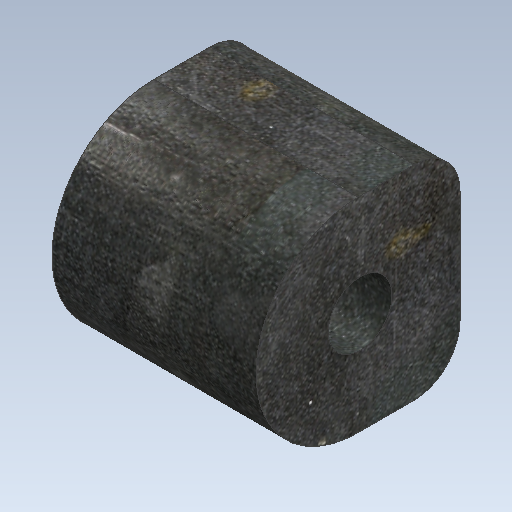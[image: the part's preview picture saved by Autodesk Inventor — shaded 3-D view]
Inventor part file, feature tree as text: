
AUTODESK INVENTOR PART (.ipt)
format: ipt  version: 2021 (Build 250183000, 183)  size: 340,992 bytes
history: native  units: mm
features: extrude x2, fillet x2, sketch x2
ambient origin geometry x8: Origin, YZ Plane, XZ Plane, XY Plane, X Axis, Y Axis, Z Axis, Center Point
bodies: Body1 (feature_tree)
feature tree (6):
  extrude  "Wyciągnięcie proste3"  Depth=80.0mm
  fillet  "Zaokrąglenie2"  Radius=80.0mm
  fillet  "Zaokrąglenie3"  Radius=80.0mm
  extrude  "Wyciągnięcie proste4"  Depth=18.0mm
  sketch  "Szkic3"
  sketch  "Szkic4"
